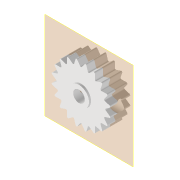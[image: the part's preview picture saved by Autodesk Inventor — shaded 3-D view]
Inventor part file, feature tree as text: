
AUTODESK INVENTOR PART (.ipt)
format: ipt  version: 2022 (Build 260153000, 153)  size: 214,016 bytes
history: native  units: mm
features: extrude x4, sketch x4, plane x1, fillet x1, pattern_circular x1
ambient origin geometry x8: Origin, YZ Plane, XZ Plane, XY Plane, X Axis, Y Axis, Z Axis, Center Point
bodies: Volumenkörper1 (feature_tree)
feature tree (11):
  extrude  "Extrusion1"  Depth=15.0mm
  plane  "Arbeitsebene1"
  extrude  "Extrusion2"  Depth=5.0mm TaperAngle=0.0deg
  extrude  "Extrusion4"  Depth=0.5mm TaperAngle=0.0deg
  fillet  "Rundung2"  Radius=9.599311mm
  pattern_circular  "Runde Anordnung3"  [2 undecoded]
  extrude  "Extrusion5"  Depth=2.5mm TaperAngle=360.0deg
  sketch  "Skizze1"  dims[d0=2.9mm d1=15.0mm]
  sketch  "Skizze2"  dims[d2=5.0mm d3=0.0mm d6=5.0mm d7=0.0mm]
  sketch  "Skizze5"  dims[d14=5.0mm d15=0.5mm d16=0.0mm d17=9.599311mm]
  sketch  "Skizze6"  dims[d18=21.816616mm d22=0.25mm d23=200.0mm d24=360.0deg d26=2.5mm d27=2.8mm d28=0.0mm d29=0.0mm]
note: 2 required parameter values undecoded (feature->parameter linkage not recoverable at this tier; creation-order binding heuristic only, values carry confidence <= 0.55)
